# Revit family: IS_Gusto_BD424_BIM_NL
name_source: partatom
category: Plumbing Fixtures
units: mm (PartAtom-declared; Revit-internal decimal feet)

## family parameters
Always vertical = No
Cut with Voids When Loaded = No
OmniClass Number = 23.45.55.17
OmniClass Title = Mixing Faucets
Part Type = Normal
Room Calculation Point = No
Round Connector Dimension = Use Diameter
Shared = No
Work Plane-Based = No

## types (5) — shared parameters
Accessories = https://www.idealstandard.nl
Afmetingen = 180 x 283 x 464 mm
AfstandsEenheid = Millimeter
AreaUnits = millimetres
AssetType = Fixed
Auteur = Ideal Standard
BIMObjectName = IS_IdealStandard_Sinktaps_Gusto_BD424
BIMobject category = Taps & Mixers
BIMobject category code = sanitary-taps-mixers
BIMobject main category = Sanitary
BIMobject main category code = sanitary
Bedieningkraan = Einhebel
Bedieningkraanwerk = Einhebel
BeschrijvingBovenkantKraan = 2 Funktionen
Beschrijvinggarantie = Herstellergarantie
Bestanddelen = https://www.idealstandard.nl
BimObjectNaam = IS_IdealStandard_Sinktaps_Gusto_BD424
Brand = Ideal Standard
Brand url = http://www.idealstandard.nl
Breedte = 179.937347
Category = Taps & Mixers
ConnectionType = Plumbing
CurrencyUnit = €
CurrentRevision = 1
Date of publishing = 19/08/2022
Diepte = 283 mm
DurationUnit = Years
DuurEenheid = Jahre
Edition number = 1
ExpectedLife = 5
FaucetFunction = Sink Mixer
FaucetOperation = Single Lever Sink Mixer
FaucetType = Sink Mixer
Functiekraanwerk = Küchenmischer
GTIN code = https://3800861109020
Garantieunits = Jahre
Help = https://www.idealstandard.nl
Hoogte = 463.64389917301
Hulp = https://www.idealstandard.nl
IFC Classification = Sanitary Terminal
IfcExportAs = IfcValveType
IfcExportType = FAUCET
Installatieinstructies = https://www.idealstandard.nl
Installation instructions = https://www.idealstandard.nl
InstallationInstructions = https://www.idealstandard.nl
Lengte = 283 mm
LinearUnits = millimetres
MaintenanceInformation = https://www.idealstandard.nl
Manufacturer = Ideal Standard
Manufacturer name = Ideal Standard
ManufacturerURL = http://www.idealstandard.nl
Masterformat 2014 Code = 22 41 16.16
Masterformat 2014 Description = Residential Sink
Materiaal = Messing
Material = Brass
Material main = Brass
Merk = Ideal Standard
NBS Reference Code = 45-35-70/345
NBS Reference Description = Water supply fittings for sinks
Name = Sinktaps_Gusto_BD424_IdealStandard
NettWeight = 2.98 Kg
Nettogewicht = 2.98
NominalDepth = 283 mm
NominalHeight = 464 mm
NominalLength = 283 mm
NominalWidth = 180 mm
Normen = Sinktaps_Gusto_BD424_IdealStandard
OmniClass Code = 23-31 11 00
OmniClass Description = Faucets
OppervlakteEenheid = Millimeter
PredefinedType = Taps & Mixers
Product Guid = 9cbc8c4a-fd9e-4171-8740-5b275d0b1617
Product SKU = BD424
Product certification = https://www.idealstandard.nl
Product data url = https://bimobject.com
Product family = Gusto
Product group = Taps & Mixers
Product name = GUSTO SINK MIXER 2 HOLES P/D 2 FUNTIONS
Product url = https://www.idealstandard.nl
ProductInformation = https://www.idealstandard.nl
Productinformatie = https://www.idealstandard.nl
QR code = http://bimobject.com
Revisie = 1
Shape = Cylindrical
Size = 180 x 283 x 464 mm
Space = Internal
SpareParts = https://www.idealstandard.nl
Technical description = https://www.idealstandard.nl
Telefoonnummer = (0228) 521-580
Toepassing = Küchenmischer
Type Comments = Plumbing
Typeconnectie = Installation
Typekraanwerk = Einhebelmischer
UNSPSC Code = 301815
URL = https://www.idealstandard.nl
Uniclass 2015 Code = Pr_40_20_87_82
Uniclass 2015 Name = Sink manual water supply sets
Uniclass2015Beschrijving = Sink manual water supply sets
Uniclass2015Code = Pr_40_20_87_84
Uniclass2015Referentie = Pr_40_20_87_82
Uniclass2015Title = Sink taps
Uniclass2015Version = v1.26
Urlproducent = https://www.idealstandard.nl
ValutaEenheid = Euro
Versie = 1
Version = 1
VolumeUnits = Liters
Volumeunits = Liter
Vorm = Zylinder
WRASURL = https://www.wrasapprovals.co.uk
WarrantyDescription = manufacturer warranty
WarrantyDurationParts = 5
WarrantyDurationUnit = Years
WarrantyStartDate = 19/08/2022
Weight Net (Kg) = 2.98
Wisselstukken = https://www.idealstandard.nl
Youtube clip = https://www.youtube.com
zero-valued in all types: BrutoGewicht, Cost, Vervangingskosten

## per-type parameters (varying)
| type | Afwerking | Artikelnummer | Artikelomschrijving | Artikelreferentie | BarCode | Barcode | Color | Description | Eigenschappen | FaucetTopDescription | Features | Finish | Kleur | MainColor | Model | ModelNumber | ModelReference |
| BD424J4 - Gusto sink mixer 2 holes p/d 2 funtions- Brushed Copper | Gebürstetes Kupfer | BD424J4 | Gusto Spültischmischer 2 Löcher p/d 2 funtions- Brushed Copper | Gusto Spültischmischer 2 Löcher p/d 2 funtions- Brushed Copper | 3800861109358 | 3800861109358 | Brushed Copper | Gusto sink mixer 2 holes p/d 2 funtions- Brushed Copper | Spültischmischer 2 Löcher p/d 2 funtions- Brushed Copper | C spout | Sink mixer 2 holes p/d 2 funtions- Brushed Copper | Brushed Copper | Gebürstetes Kupfer | Brushed Copper | BD424J4 | BD424J4 | Gusto sink mixer 2 holes p/d 2 funtions- Brushed Copper |
| BD424GN - Gusto sink mixer 2 holes p/d 2 funtions- Silver | Silber | BD424GN | Gusto Spültischmischer 2 Löcher p/d 2 funtions- Silber | Gusto Spültischmischer 2 Löcher p/d 2 funtions- Silber | 3800861109013 | 3800861109013 | Silver | Gusto sink mixer 2 holes p/d 2 funtions- Silver | Spültischmischer 2 Löcher p/d 2 funtions- Silber | Single lever | Sink mixer 2 holes p/d 2 funtions- Silver | Silver | Silber | Silver | BD424GN | BD424GN | Gusto sink mixer 2 holes p/d 2 funtions- Silver |
| BD424AA - Gusto slim sink mixer 2 holes p/d 2 funtions- Chrome | Chrom | BD424AA | Gusto Slim Spültischmischer 2 Löcher p/d 2 Funktionen - Chrom | Gusto Slim Spültischmischer 2 Löcher p/d 2 Funktionen - Chrom | 3800861108955 | 3800861108955 | Chrome | Gusto slim sink mixer 2 holes p/d 2 funtions- Chrome | Slim Spültischmischer 2 Löcher p/d 2 Funktionen - Chrom | C spout | Slim Sink mixer 2 holes p/d 2 funtions- Chrome | Chrome | Chrom | Chrome | BD424AA | BD424AA | Gusto slim sink mixer 2 holes p/d 2 funtions- Chrome |
| BD424A5 - Gusto sink mixer 2 holes p/d 2 funtions- Magnetic Grey | Magnetisches Grau | BD424A5 | Gusto Spültischmischer 2 Löcher p/d 2 funtions- Magnetic Grey | Gusto Spültischmischer 2 Löcher p/d 2 funtions- Magnetic Grey | 3800861109198 | 3800861109198 | Magnetic Grey | Gusto sink mixer 2 holes p/d 2 funtions- Magnetic Grey | Spültischmischer 2 Löcher p/d 2 funtions- Magnetic Grey | C spout | Sink mixer 2 holes p/d 2 funtions- Magnetic Grey | Magnetic Grey | Magnetisches Grau | Magnetic Grey | BD424A5 | BD424A5 | Gusto sink mixer 2 holes p/d 2 funtions- Magnetic Grey |
| BD424A2 - Gusto sink mixer 2 holes p/d 2 funtions- BrushedGold | Gebürstetes Gold | BD424A2 | Gusto Spültischmischer 2 Löcher p/d 2 funtions- BrushedGold | Gusto Spültischmischer 2 Löcher p/d 2 funtions- BrushedGold | 3800861109020 | 3800861109020 | BrushedGold | Gusto sink mixer 2 holes p/d 2 funtions- BrushedGold | Spültischmischer 2 Löcher p/d 2 funtions- BrushedGold | Single lever | Sink mixer 2 holes p/d 2 funtions- BrushedGold | BrushedGold | Gebürstetes Gold | BrushedGold | BD424A2 | BD424A2 | Gusto sink mixer 2 holes p/d 2 funtions- BrushedGold |

## geometry (parser evidence)
native form markers: Sweep x2
no freeform markers — native parametric forms only
